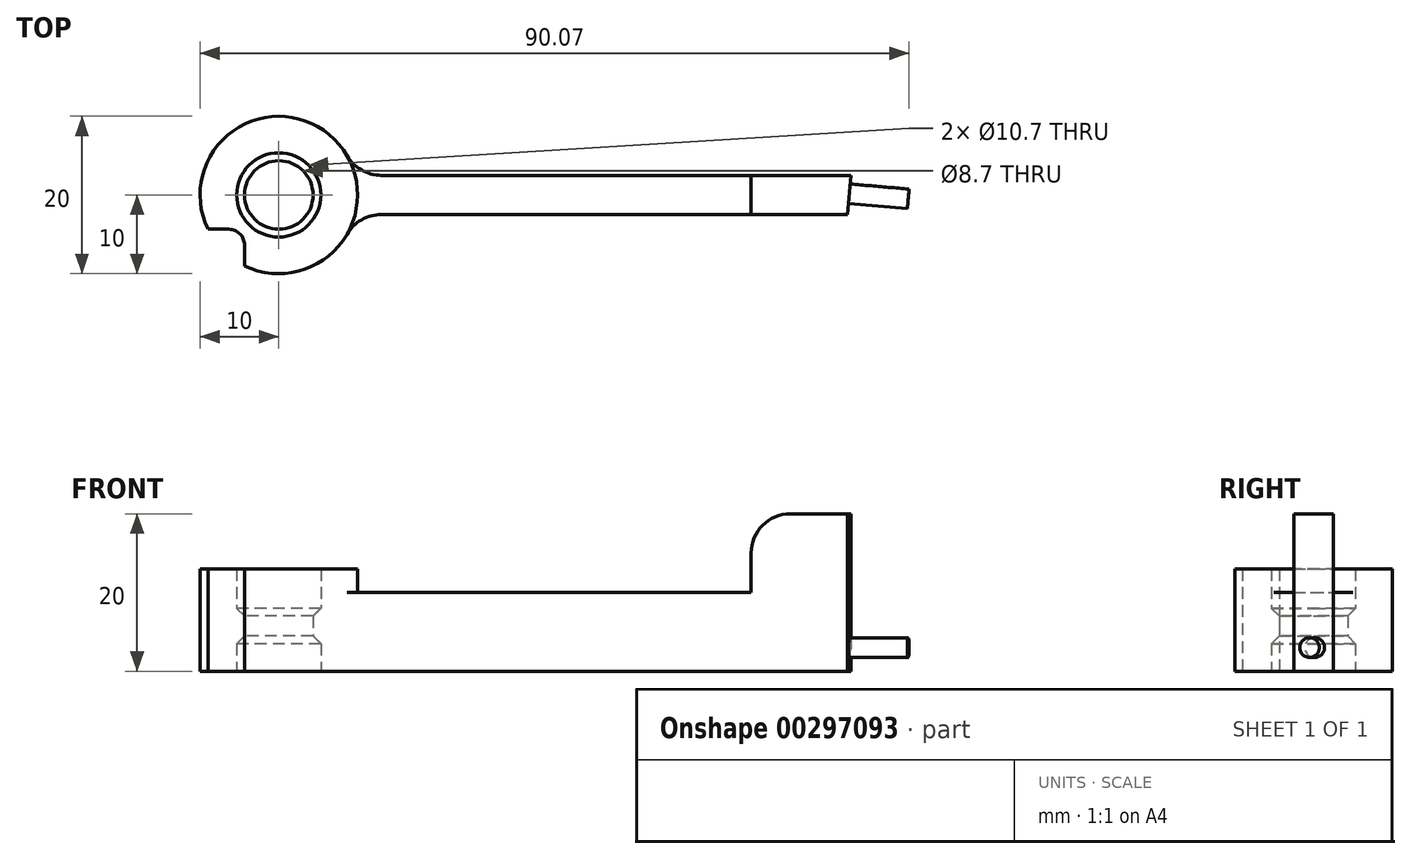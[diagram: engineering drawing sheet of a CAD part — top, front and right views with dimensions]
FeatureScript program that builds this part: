
annotation { "Feature Type Name" : "Feature", "Feature Type Description" : "" }
export const myFeature = defineFeature(function(context is Context, id is Id, definition is map)
    precondition{}
    {
        {
            var Q0;
            Q0=qCreatedBy(makeId("Top.planeOp"),FACE);
            var sketch = newSketch(context, id + "F0", { "sketchPlane" : qUnion([Q0])});
            skCircle(sketch, "E0", {"center": v(0, 0) * mm, "radius": 5.35 * mm});
            skCircle(sketch, "E1", {"center": v(0, 0) * mm, "radius": 10 * mm});
            skLineSegment(sketch, "E2", {"start": v(-4.35, 9) * mm, "end": v(-4.35, 6.35) * mm});
            skLineSegment(sketch, "E3", {"start": v(-6.35, 4.35) * mm, "end": v(-9, 4.35) * mm});
            skPoint(sketch, "E4.visualSharp", {"position": v(-4.35, 4.35) * mm});
            skArc(sketch, "E4.filletArc", {"start": v(-6.35, 4.35) * mm, "mid": v(-4.94, 4.94) * mm, "end": v(-4.35, 6.35) * mm});
            skLineSegment(sketch, "E5.MirrorCS", {"start": v(6.35, 4.35) * mm, "end": v(9, 4.35) * mm});
            skLineSegment(sketch, "E6.MirrorCS", {"start": v(4.35, 9) * mm, "end": v(4.35, 6.35) * mm});
            skArc(sketch, "E7.MirrorCS", {"start": v(6.35, 4.35) * mm, "mid": v(4.94, 4.94) * mm, "end": v(4.35, 6.35) * mm});
            skPoint(sketch, "E8.MirrorP", {"position": v(4.35, 4.35) * mm});
            skPoint(sketch, "E9.MirrorP", {"position": v(-4.35, -4.35) * mm});
            skArc(sketch, "E10.MirrorCS", {"start": v(-6.35, -4.35) * mm, "mid": v(-4.94, -4.94) * mm, "end": v(-4.35, -6.35) * mm});
            skLineSegment(sketch, "E11.MirrorCS", {"start": v(-6.35, -4.35) * mm, "end": v(-9, -4.35) * mm});
            skLineSegment(sketch, "E12.MirrorCS", {"start": v(-4.35, -9) * mm, "end": v(-4.35, -6.35) * mm});
            skPoint(sketch, "E13.MirrorP", {"position": v(4.35, -4.35) * mm});
            skLineSegment(sketch, "E14.MirrorCS", {"start": v(6.35, -4.35) * mm, "end": v(9, -4.35) * mm});
            skArc(sketch, "E15.MirrorCS", {"start": v(6.35, -4.35) * mm, "mid": v(4.94, -4.94) * mm, "end": v(4.35, -6.35) * mm});
            skLineSegment(sketch, "E16.MirrorCS", {"start": v(4.35, -9) * mm, "end": v(4.35, -6.35) * mm});
            skLineSegment(sketch, "E17", {"start": v(9.68, 2.5) * mm, "end": v(77.55, 2.5) * mm});
            skLineSegment(sketch, "E18", {"start": v(9.68, -2.5) * mm, "end": v(77.55, -2.5) * mm});
            skLineSegment(sketch, "E19", {"start": v(20.32, 2.5) * mm, "end": v(20.32, -2.5) * mm, "construction": true});
            skPoint(sketch, "E20", {"position": v(20.32, 0) * mm});
            skCircle(sketch, "E21", {"center": v(80, 0) * mm, "radius": 3.5 * mm});
            skLineSegment(sketch, "E22", {"start": v(80.3, 3.49) * mm, "end": v(80, 0) * mm});
            skLineSegment(sketch, "E23", {"start": v(80, 0) * mm, "end": v(79.7, -3.49) * mm});
            skLineSegment(sketch, "E24", {"start": v(80, 0) * mm, "end": v(80, 12.25) * mm, "construction": true});
            skCircle(sketch, "E25", {"center": v(0, 0) * mm, "radius": 4.35 * mm});
            skLineSegment(sketch, "E26", {"start": v(60, 2.5) * mm, "end": v(60, -2.5) * mm});
            skSolve(sketch);
        }
        {
            var Q0;
            {var subQ0=sQuery(id+"F0.wireOp",EDGE,"E2");Q0=makeQuery(id+"F0.imprint","IMPRINT",FACE,{"disambiguationData":[TD([[makeQuery(id+"F0.imprint","IMPRINT",EDGE,{"derivedFrom":subQ0}),-1.0]])]});}
            var Q1;
            Q1=makeQuery(id+"F0.imprint","IMPRINT",FACE,{"disambiguationData":[TD([[makeQuery(id+"F0.imprint","IMPRINT",EDGE,{"derivedFrom":sQuery(id+"F0.wireOp",EDGE,"E0")}),-1.0]])]});
            var Q2;
            Q2=makeQuery(id+"F0.imprint","IMPRINT",FACE,{"disambiguationData":[TD([[makeQuery(id+"F0.imprint","IMPRINT",EDGE,{"derivedFrom":sQuery(id+"F0.wireOp",EDGE,"E10.MirrorCS")}),-1.0]])]});
            var Q3;
            {var subQ0=sQuery(id+"F0.wireOp",EDGE,"E14.MirrorCS");Q3=makeQuery(id+"F0.imprint","IMPRINT",FACE,{"disambiguationData":[TD([[makeQuery(id+"F0.imprint","IMPRINT",EDGE,{"derivedFrom":subQ0}),-1.0]])]});}
            var Q4;
            {var subQ0=sQuery(id+"F0.wireOp",EDGE,"E5.MirrorCS");Q4=makeQuery(id+"F0.imprint","IMPRINT",FACE,{"disambiguationData":[TD([[makeQuery(id+"F0.imprint","IMPRINT",EDGE,{"derivedFrom":subQ0}),1.0]])]});}
            var Q5;
            {var subQ0=sQuery(id+"F0.wireOp",EDGE,"E17");Q5=makeQuery(id+"F0.imprint","IMPRINT",FACE,{"disambiguationData":[TD([[makeQuery(id+"F0.imprint","IMPRINT",EDGE,{"derivedFrom":subQ0}),-1.0]])]});}
            var Q6;
            {var subQ0=sQuery(id+"F0.wireOp",EDGE,"E22");Q6=makeQuery(id+"F0.imprint","IMPRINT",FACE,{"disambiguationData":[TD([[makeQuery(id+"F0.imprint","IMPRINT",EDGE,{"derivedFrom":subQ0}),-1.0]])]});}
            extrude(context, id + "F1", {"entities" : qUnion([Q0, Q1, Q2, Q3, Q4, Q5, Q6]), "depth" : 10 * mm});
        }
        {
            var Q0;
            Q0=makeQuery(id+"F0.imprint","IMPRINT",FACE,{"disambiguationData":[TD([[makeQuery(id+"F0.imprint","IMPRINT",EDGE,{"derivedFrom":sQuery(id+"F0.wireOp",EDGE,"E0")}),1.0]])]});
            extrude(context, id + "F2", {"entities" : qUnion([Q0]), "operationType" : NewBodyOperationType.ADD, "depth" : 8 * mm, "hasSecondDirection" : true, "secondDirectionOppositeDirection" : false, "secondDirectionDepth" : 3.5 * mm});
        }
        {
            var Q0;
            Q0=makeQuery(id+"F2.opExtrude","CAP_EDGE",EDGE,{"disambiguationData":[OSD([sQuery(id+"F0.wireOp",EDGE,"E25")])],"isStart":true});
            var Q1;
            Q1=makeQuery(id+"F2.opExtrude","CAP_EDGE",EDGE,{"disambiguationData":[OSD([sQuery(id+"F0.wireOp",EDGE,"E25")])],"isStart":false});
            chamfer(context, id + "F3", {"entities" : qUnion([Q0, Q1]), "width" : 1 * mm, "tangentPropagation" : true});
        }
        {
            var Q0;
            Q0=makeQuery(id+"F0.imprint","IMPRINT",FACE,{"disambiguationData":[TD([[makeQuery(id+"F0.imprint","IMPRINT",EDGE,{"derivedFrom":sQuery(id+"F0.wireOp",EDGE,"E10.MirrorCS")}),-1.0]])]});
            var Q1;
            {var subQ0=sQuery(id+"F0.wireOp",EDGE,"E14.MirrorCS");Q1=makeQuery(id+"F0.imprint","IMPRINT",FACE,{"disambiguationData":[TD([[makeQuery(id+"F0.imprint","IMPRINT",EDGE,{"derivedFrom":subQ0}),-1.0]])]});}
            var Q2;
            {var subQ0=sQuery(id+"F0.wireOp",EDGE,"E5.MirrorCS");Q2=makeQuery(id+"F0.imprint","IMPRINT",FACE,{"disambiguationData":[TD([[makeQuery(id+"F0.imprint","IMPRINT",EDGE,{"derivedFrom":subQ0}),1.0]])]});}
            var Q3;
            {var subQ0=sQuery(id+"F0.wireOp",EDGE,"E2");Q3=makeQuery(id+"F0.imprint","IMPRINT",FACE,{"disambiguationData":[TD([[makeQuery(id+"F0.imprint","IMPRINT",EDGE,{"derivedFrom":subQ0}),-1.0]])]});}
            extrude(context, id + "F4", {"entities" : qUnion([Q0, Q1, Q2, Q3]), "operationType" : NewBodyOperationType.ADD, "depth" : 13 * mm});
        }
        {
            var Q0;
            {var subQ0=sQuery(id+"F0.wireOp",EDGE,"E22");Q0=makeQuery(id+"F0.imprint","IMPRINT",FACE,{"disambiguationData":[TD([[makeQuery(id+"F0.imprint","IMPRINT",EDGE,{"derivedFrom":subQ0}),-1.0]])]});}
            var Q1;
            {var subQ3=sQuery(id+"F0.wireOp",EDGE,"E26");Q1=makeQuery(id+"F0.imprint","IMPRINT",FACE,{"disambiguationData":[TD([[makeQuery(id+"F0.imprint","IMPRINT",EDGE,{"derivedFrom":subQ3}),1.0]])]});}
            extrude(context, id + "F5", {"entities" : qUnion([Q0, Q1]), "operationType" : NewBodyOperationType.ADD, "depth" : 20 * mm});
        }
        {
            var Q0;
            {var subQ0=sQuery(id+"F0.wireOp",EDGE,"E23");var subQ1=sQuery(id+"F0.wireOp",EDGE,"E22");Q0=makeQuery(id+"F5.boolean.opBoolean","MERGE",FACE,{"derivedFrom":[makeQuery(id+"F1.opExtrude","SWEPT_FACE",FACE,{"disambiguationData":[OSD([subQ1,subQ0])]}),makeQuery(id+"F5.opExtrude","SWEPT_FACE",FACE,{"disambiguationData":[OSD([subQ1,subQ0])]})]});}
            var sketch = newSketch(context, id + "F6", { "sketchPlane" : qUnion([Q0])});
            skCircle(sketch, "E27", {"center": v(6.47, 17) * mm, "radius": 1.25 * mm});
            skPoint(sketch, "E28", {"position": v(10.47, 10) * mm});
            skPoint(sketch, "E29", {"position": v(3.47, 10) * mm});
            skLineSegment(sketch, "E30", {"start": v(10.47, 10) * mm, "end": v(3.47, 10) * mm, "construction": true});
            skCircle(sketch, "E31.MirrorC", {"center": v(6.47, 3) * mm, "radius": 1.25 * mm});
            skSolve(sketch);
        }
        {
            var Q0;
            Q0=makeQuery(id+"F6.imprint","IMPRINT",FACE,{"disambiguationData":[TD([[makeQuery(id+"F6.imprint","IMPRINT",EDGE,{"derivedFrom":sQuery(id+"F6.wireOp",EDGE,"E27")}),1.0]])]});
            var Q1;
            Q1=makeQuery(id+"F6.imprint","IMPRINT",FACE,{"disambiguationData":[TD([[makeQuery(id+"F6.imprint","IMPRINT",EDGE,{"derivedFrom":sQuery(id+"F6.wireOp",EDGE,"E31.MirrorC")}),-1.0]])]});
            extrude(context, id + "F7", {"entities" : qUnion([Q0, Q1]), "operationType" : NewBodyOperationType.REMOVE, "oppositeDirection" : true, "depth" : 7.5 * mm});
        }
        {
            var Q0;
            {var subQ0=sQuery(id+"F0.wireOp",EDGE,"E21");Q0=makeQuery(id+"F5.boolean.opBoolean","INTERSECT",EDGE,{"derivedFrom":[makeQuery(id+"F1.opExtrude","CAP_FACE",FACE,{"disambiguationData":[OSD([sQuery(id+"F0.wireOp",EDGE,"E0"),sQuery(id+"F0.wireOp",EDGE,"E1"),sQuery(id+"F0.wireOp",EDGE,"E17"),sQuery(id+"F0.wireOp",EDGE,"E18"),subQ0,sQuery(id+"F0.wireOp",EDGE,"E22"),sQuery(id+"F0.wireOp",EDGE,"E23")])],"isStart":false}),makeQuery(id+"F5.opExtrude","SWEPT_FACE",FACE,{"disambiguationData":[OSD([subQ0])]})]});}
            var Q1;
            Q1=makeQuery(id+"F1.opExtrude","SWEPT_EDGE",EDGE,{"disambiguationData":[OSD([sQuery(id+"F0.wireOp",EDGE,"E1"),sQuery(id+"F0.wireOp",EDGE,"E17")])]});
            var Q2;
            Q2=makeQuery(id+"F1.opExtrude","SWEPT_EDGE",EDGE,{"disambiguationData":[OSD([sQuery(id+"F0.wireOp",EDGE,"E1"),sQuery(id+"F0.wireOp",EDGE,"E18")])]});
            var Q3;
            Q3=makeQuery(id+"F1.opExtrude","SWEPT_EDGE",EDGE,{"disambiguationData":[OSD([sQuery(id+"F0.wireOp",EDGE,"E17"),sQuery(id+"F0.wireOp",EDGE,"E21")])]});
            var Q4;
            Q4=makeQuery(id+"F1.opExtrude","SWEPT_EDGE",EDGE,{"disambiguationData":[OSD([sQuery(id+"F0.wireOp",EDGE,"E18"),sQuery(id+"F0.wireOp",EDGE,"E21")])]});
            var Q5;
            Q5=makeQuery(id+"F5.opExtrude","CAP_EDGE",EDGE,{"disambiguationData":[OSD([sQuery(id+"F0.wireOp",EDGE,"E26")])],"isStart":false});
            fillet(context, id + "F8", {"entities" : qUnion([Q0, Q1, Q2, Q3, Q4, Q5]), "radius" : 5 * mm, "tangentPropagation" : true, "allowEdgeOverflow" : false});
        }
    });
